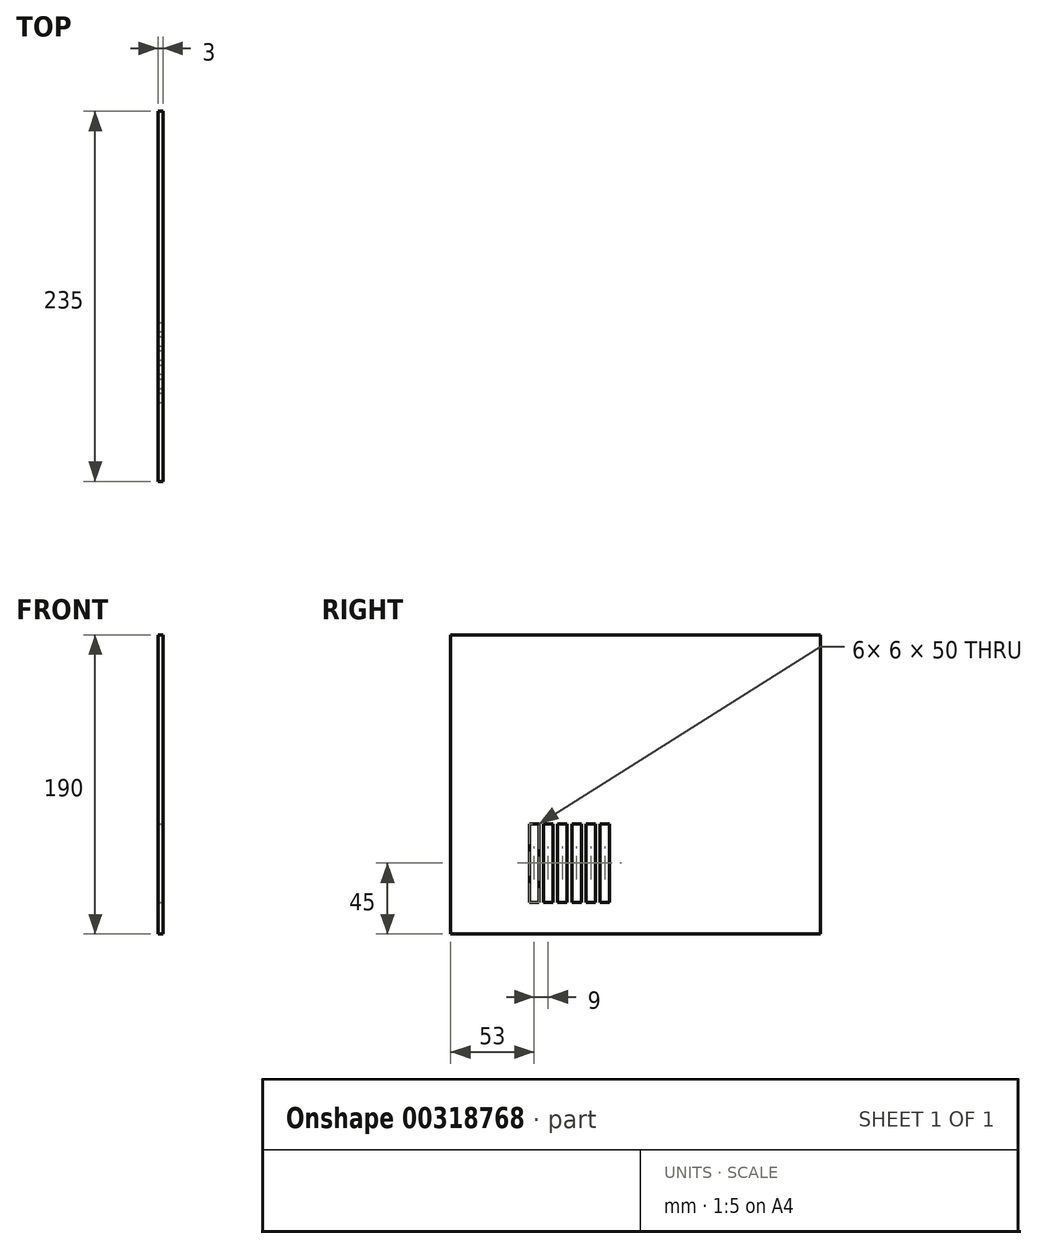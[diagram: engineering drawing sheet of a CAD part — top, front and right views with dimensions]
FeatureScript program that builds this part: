
annotation { "Feature Type Name" : "Feature", "Feature Type Description" : "" }
export const myFeature = defineFeature(function(context is Context, id is Id, definition is map)
    precondition{}
    {
        {
            var Q0;
            Q0=qCreatedBy(makeId("Right.planeOp"),FACE);
            var sketch = newSketch(context, id + "F0", { "sketchPlane" : qUnion([Q0])});
            skLineSegment(sketch, "E0.bottom", {"start": v(117.5, -95) * mm, "end": v(-117.5, -95) * mm});
            skLineSegment(sketch, "E0.top", {"start": v(117.5, 95) * mm, "end": v(-117.5, 95) * mm});
            skLineSegment(sketch, "E0.left", {"start": v(117.5, -95) * mm, "end": v(117.5, 95) * mm});
            skLineSegment(sketch, "E0.right", {"start": v(-117.5, -95) * mm, "end": v(-117.5, 95) * mm});
            skPoint(sketch, "E0.middle", {"position": v(0, 0) * mm});
            skSolve(sketch);
        }
        {
            var Q0;
            Q0=makeQuery(id+"F0.imprint","IMPRINT",FACE,{"disambiguationData":[TD([[makeQuery(id+"F0.imprint","IMPRINT",EDGE,{"derivedFrom":sQuery(id+"F0.wireOp",EDGE,"E0.bottom")}),-1.0]])]});
            extrude(context, id + "F1", {"entities" : qUnion([Q0]), "depth" : 3 * mm, "offsetDistance" : 25 * mm});
        }
        {
            var Q0;
            Q0=makeQuery(id+"F1.opExtrude","CAP_FACE",FACE,{"disambiguationData":[OSD([sQuery(id+"F0.wireOp",EDGE,"E0.bottom"),sQuery(id+"F0.wireOp",EDGE,"E0.top"),sQuery(id+"F0.wireOp",EDGE,"E0.left"),sQuery(id+"F0.wireOp",EDGE,"E0.right")])],"isStart":false});
            var sketch = newSketch(context, id + "F2", { "sketchPlane" : qUnion([Q0])});
            skLineSegment(sketch, "E1.bottom", {"start": v(-61.5, -75) * mm, "end": v(-67.5, -75) * mm});
            skLineSegment(sketch, "E1.top", {"start": v(-61.5, -25) * mm, "end": v(-67.5, -25) * mm});
            skLineSegment(sketch, "E1.left", {"start": v(-61.5, -75) * mm, "end": v(-61.5, -25) * mm});
            skLineSegment(sketch, "E1.right", {"start": v(-67.5, -75) * mm, "end": v(-67.5, -25) * mm});
            skPoint(sketch, "E1.middle", {"position": v(-64.5, -50) * mm});
            skLineSegment(sketch, "E2.1.0.0", {"start": v(-52.5, -75) * mm, "end": v(-52.5, -25) * mm});
            skLineSegment(sketch, "E2.1.0.1", {"start": v(-52.5, -75) * mm, "end": v(-58.5, -75) * mm});
            skLineSegment(sketch, "E2.1.0.2", {"start": v(-58.5, -75) * mm, "end": v(-58.5, -25) * mm});
            skLineSegment(sketch, "E2.1.0.3", {"start": v(-52.5, -25) * mm, "end": v(-58.5, -25) * mm});
            skLineSegment(sketch, "E2.2.0.0", {"start": v(-43.5, -75) * mm, "end": v(-43.5, -25) * mm});
            skLineSegment(sketch, "E2.2.0.1", {"start": v(-43.5, -75) * mm, "end": v(-49.5, -75) * mm});
            skLineSegment(sketch, "E2.2.0.2", {"start": v(-49.5, -75) * mm, "end": v(-49.5, -25) * mm});
            skLineSegment(sketch, "E2.2.0.3", {"start": v(-43.5, -25) * mm, "end": v(-49.5, -25) * mm});
            skLineSegment(sketch, "E2.3.0.0", {"start": v(-34.5, -75) * mm, "end": v(-34.5, -25) * mm});
            skLineSegment(sketch, "E2.3.0.1", {"start": v(-34.5, -75) * mm, "end": v(-40.5, -75) * mm});
            skLineSegment(sketch, "E2.3.0.2", {"start": v(-40.5, -75) * mm, "end": v(-40.5, -25) * mm});
            skLineSegment(sketch, "E2.3.0.3", {"start": v(-34.5, -25) * mm, "end": v(-40.5, -25) * mm});
            skLineSegment(sketch, "E2.4.0.0", {"start": v(-25.5, -75) * mm, "end": v(-25.5, -25) * mm});
            skLineSegment(sketch, "E2.4.0.1", {"start": v(-25.5, -75) * mm, "end": v(-31.5, -75) * mm});
            skLineSegment(sketch, "E2.4.0.2", {"start": v(-31.5, -75) * mm, "end": v(-31.5, -25) * mm});
            skLineSegment(sketch, "E2.4.0.3", {"start": v(-25.5, -25) * mm, "end": v(-31.5, -25) * mm});
            skLineSegment(sketch, "E2.5.0.0", {"start": v(-16.5, -75) * mm, "end": v(-16.5, -25) * mm});
            skLineSegment(sketch, "E2.5.0.1", {"start": v(-16.5, -75) * mm, "end": v(-22.5, -75) * mm});
            skLineSegment(sketch, "E2.5.0.2", {"start": v(-22.5, -75) * mm, "end": v(-22.5, -25) * mm});
            skLineSegment(sketch, "E2.5.0.3", {"start": v(-16.5, -25) * mm, "end": v(-22.5, -25) * mm});
            skLineSegment(sketch, "E2.direction1", {"start": v(-61.5, -75) * mm, "end": v(-52.5, -75) * mm, "construction": true});
            skSolve(sketch);
        }
        {
            var Q0;
            Q0=makeQuery(id+"F2.imprint","IMPRINT",FACE,{"disambiguationData":[TD([[makeQuery(id+"F2.imprint","IMPRINT",EDGE,{"derivedFrom":sQuery(id+"F2.wireOp",EDGE,"E1.bottom")}),-1.0]])]});
            var Q1;
            Q1=makeQuery(id+"F2.imprint","IMPRINT",FACE,{"disambiguationData":[TD([[makeQuery(id+"F2.imprint","IMPRINT",EDGE,{"derivedFrom":sQuery(id+"F2.wireOp",EDGE,"E2.1.0.0")}),1.0]])]});
            var Q2;
            Q2=makeQuery(id+"F2.imprint","IMPRINT",FACE,{"disambiguationData":[TD([[makeQuery(id+"F2.imprint","IMPRINT",EDGE,{"derivedFrom":sQuery(id+"F2.wireOp",EDGE,"E2.2.0.0")}),1.0]])]});
            var Q3;
            Q3=makeQuery(id+"F2.imprint","IMPRINT",FACE,{"disambiguationData":[TD([[makeQuery(id+"F2.imprint","IMPRINT",EDGE,{"derivedFrom":sQuery(id+"F2.wireOp",EDGE,"E2.3.0.0")}),1.0]])]});
            var Q4;
            Q4=makeQuery(id+"F2.imprint","IMPRINT",FACE,{"disambiguationData":[TD([[makeQuery(id+"F2.imprint","IMPRINT",EDGE,{"derivedFrom":sQuery(id+"F2.wireOp",EDGE,"E2.4.0.0")}),1.0]])]});
            var Q5;
            Q5=makeQuery(id+"F2.imprint","IMPRINT",FACE,{"disambiguationData":[TD([[makeQuery(id+"F2.imprint","IMPRINT",EDGE,{"derivedFrom":sQuery(id+"F2.wireOp",EDGE,"E2.5.0.0")}),1.0]])]});
            extrude(context, id + "F3", {"entities" : qUnion([Q0, Q1, Q2, Q3, Q4, Q5]), "operationType" : NewBodyOperationType.REMOVE, "oppositeDirection" : true, "depth" : 25 * mm, "offsetDistance" : 25 * mm});
        }
    });
